# Revit family: MDN 750 PLUS
name_source: partatom
category: Mechanical Equipment
revit_build: Autodesk Revit 2018 (Build: 20170223_1515(x64)
units: mm (PartAtom-declared; Revit-internal decimal feet)

## family parameters
Always vertical = Yes
Cut with Voids When Loaded = No
OmniClass Number = 23.75.10.14.14.11
OmniClass Title = Storage Heaters
Part Type = Normal
Room Calculation Point = No
Round Connector Dimension = Use Radius
Shared = No
Work Plane-Based = No

## types (1)
- MDN 750 PLUS
    Art. No. = 429 754 211
    Beugel = Metaal
    Breedte = 750 mm  [stored 2.46063 ft]
    Colour = Laquer White
    Diepte = 71 mm  [stored 0.23294 ft]
    Hoogte = 440 mm  [stored 1.44357 ft]
    Licht grijs = Licht grijs
    Manufacturer = Masterwatt B.V.
    Model = MDN 750 PLUS
    Phase = 1
    Power (default) = 750 VA
    Scherm = Screen
    URL = https://masterwatt.nl
    Voltage = 230 V
    Zwart = Zwart

note: [stored X ft] marks values corroborated as IEEE doubles in the binary element streams (Revit-internal decimal feet)

## geometry (parser evidence)
native form markers: Sweep x8
no freeform markers — native parametric forms only
